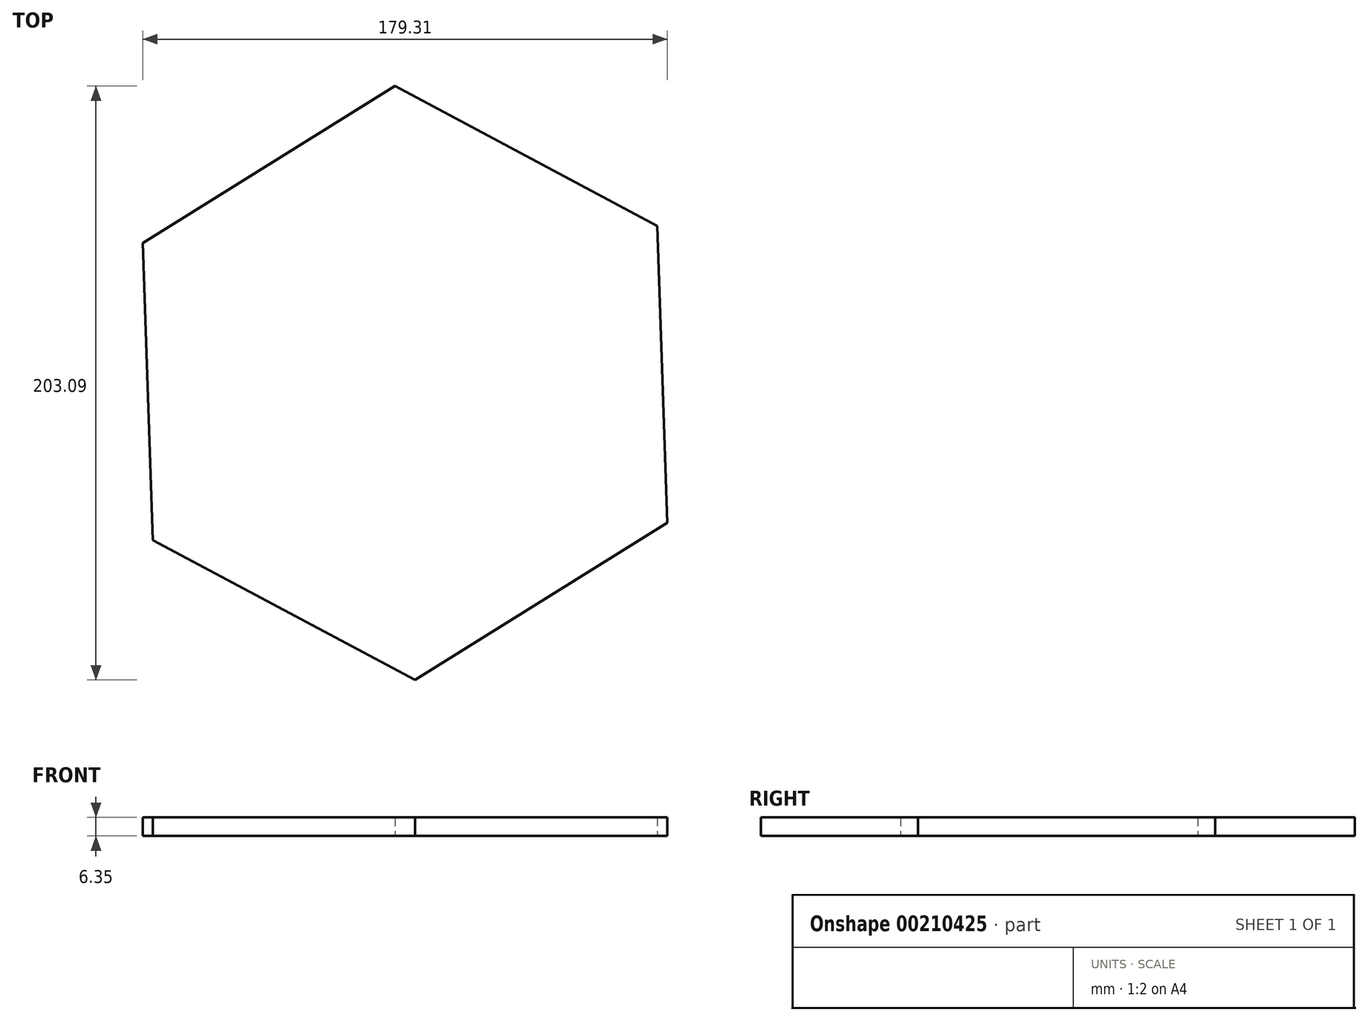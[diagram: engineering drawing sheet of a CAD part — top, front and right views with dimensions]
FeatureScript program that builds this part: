
annotation { "Feature Type Name" : "Feature", "Feature Type Description" : "" }
export const myFeature = defineFeature(function(context is Context, id is Id, definition is map)
    precondition{}
    {
        {
            var Q0;
            Q0=qCreatedBy(makeId("Top.planeOp"),FACE);
            var sketch = newSketch(context, id + "F0", { "sketchPlane" : qUnion([Q0])});
            skCircle(sketch, "E0.cCircle", {"center": v(-1.79, -0.24) * mm, "radius": 87.99 * mm, "construction": true});
            skLineSegment(sketch, "E0.0", {"start": v(87.87, -48.04) * mm, "end": v(1.64, -101.79) * mm});
            skLineSegment(sketch, "E0.1", {"start": v(1.64, -101.79) * mm, "end": v(-88, -53.99) * mm});
            skLineSegment(sketch, "E0.2", {"start": v(-88, -53.99) * mm, "end": v(-91.44, 47.56) * mm});
            skLineSegment(sketch, "E0.3", {"start": v(-91.44, 47.56) * mm, "end": v(-5.22, 101.3) * mm});
            skLineSegment(sketch, "E0.4", {"start": v(-5.22, 101.3) * mm, "end": v(84.44, 53.5) * mm});
            skLineSegment(sketch, "E0.5", {"start": v(84.44, 53.5) * mm, "end": v(87.87, -48.04) * mm});
            skPoint(sketch, "E0.0.midPoint", {"position": v(44.76, -74.91) * mm});
            skSolve(sketch);
        }
        {
            var Q0;
            Q0=makeQuery(id+"F0.imprint","IMPRINT",FACE,{"disambiguationData":[TD([[makeQuery(id+"F0.imprint","IMPRINT",EDGE,{"derivedFrom":sQuery(id+"F0.wireOp",EDGE,"E0.0")}),-1.0]])]});
            extrude(context, id + "F1", {"entities" : qUnion([Q0]), "depth" : 6.35 * mm});
        }
    });
